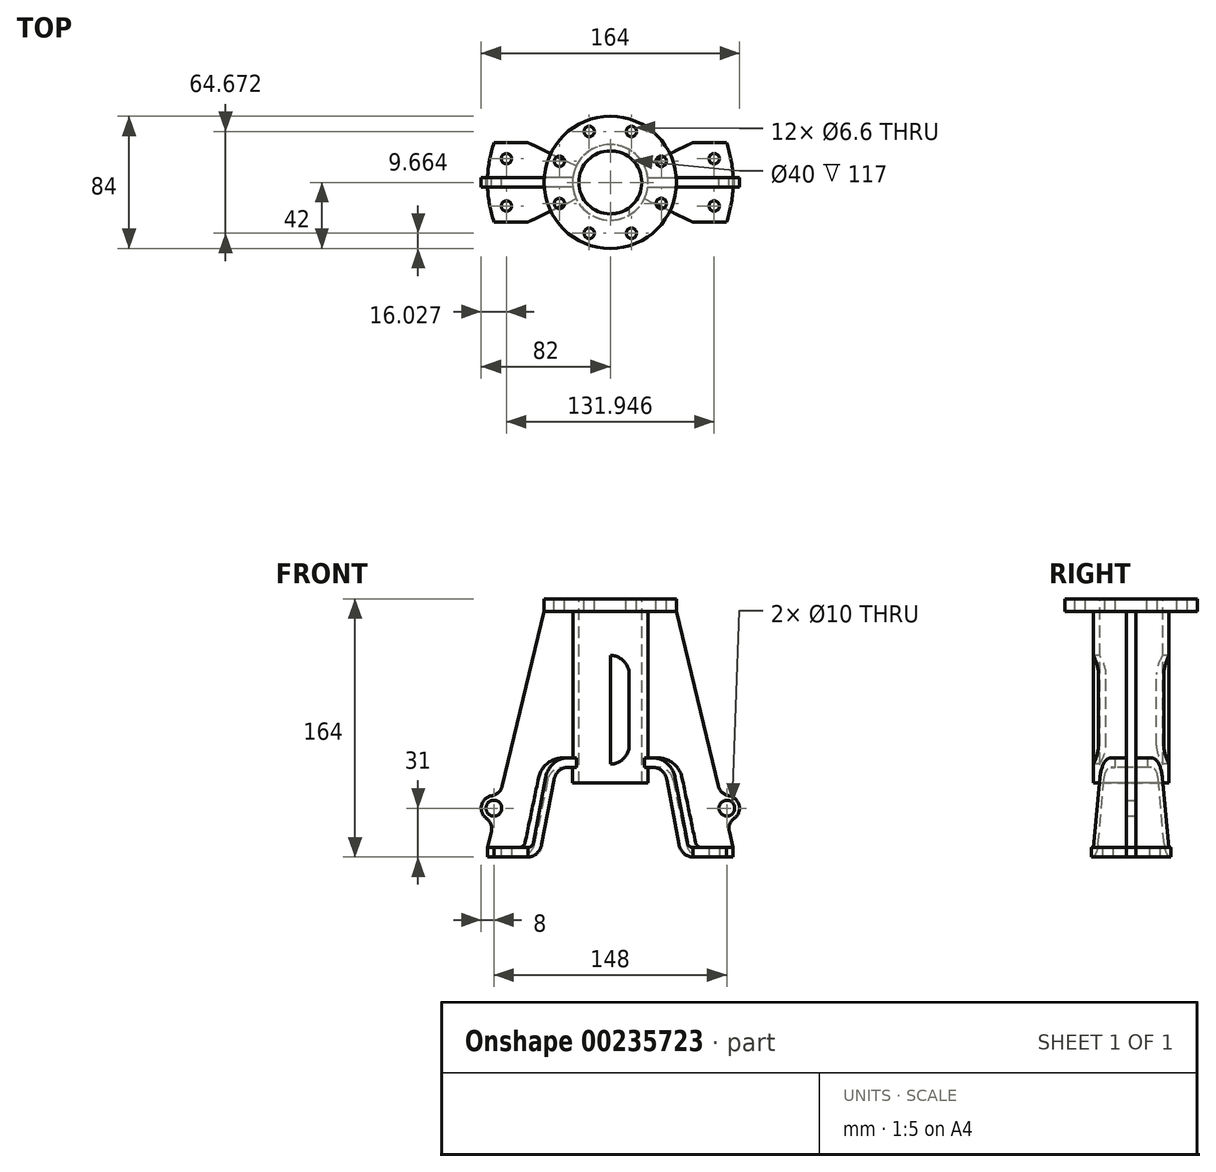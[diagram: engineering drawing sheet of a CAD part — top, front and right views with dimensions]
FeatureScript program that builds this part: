
annotation { "Feature Type Name" : "Feature", "Feature Type Description" : "" }
export const myFeature = defineFeature(function(context is Context, id is Id, definition is map)
    precondition{}
    {
        {
            var Q0;
            Q0=qCreatedBy(makeId("Front.planeOp"),FACE);
            var sketch = newSketch(context, id + "F0", { "sketchPlane" : qUnion([Q0])});
            skLineSegment(sketch, "E0.bottom", {"start": v(12, 22.5) * mm, "end": v(0, 22.5) * mm, "construction": true});
            skLineSegment(sketch, "E0.top", {"start": v(12, -22.5) * mm, "end": v(0, -22.5) * mm, "construction": true});
            skLineSegment(sketch, "E0.left", {"start": v(12, 22.5) * mm, "end": v(12, -22.5) * mm});
            skPoint(sketch, "E0.middle", {"position": v(0, 0) * mm});
            skArc(sketch, "E1", {"start": v(12, 22.5) * mm, "mid": v(8.49, 30.99) * mm, "end": v(0, 34.5) * mm});
            skArc(sketch, "E2", {"start": v(0, -34.5) * mm, "mid": v(8.49, -30.99) * mm, "end": v(12, -22.5) * mm});
            skLineSegment(sketch, "E3", {"start": v(0, 0) * mm, "end": v(0, -93.5) * mm, "construction": true});
            skPoint(sketch, "E3.endSnap0", {"position": v(0, -34.5) * mm});
            skPoint(sketch, "E4.endSnap0", {"position": v(0, 34.5) * mm});
            skLineSegment(sketch, "E5.trimOffspring", {"start": v(0, 0) * mm, "end": v(0, 70.5) * mm, "construction": true});
            skLineSegment(sketch, "E6", {"start": v(0, -93.5) * mm, "end": v(0, -36.5) * mm, "construction": true});
            skLineSegment(sketch, "E7", {"start": v(0, -93.5) * mm, "end": v(50, -93.5) * mm, "construction": true});
            skLineSegment(sketch, "E8", {"start": v(58.13, -93.5) * mm, "end": v(78, -93.5) * mm});
            skLineSegment(sketch, "E9", {"start": v(0, -36.5) * mm, "end": v(30, -36.5) * mm, "construction": true});
            skLineSegment(sketch, "E10.bottom", {"start": v(20, 70.5) * mm, "end": v(24, 70.5) * mm});
            skLineSegment(sketch, "E10.top", {"start": v(20, -46.5) * mm, "end": v(24, -46.5) * mm});
            skLineSegment(sketch, "E10.left", {"start": v(0, 70.5) * mm, "end": v(0, -46.5) * mm});
            skLineSegment(sketch, "E10.right", {"start": v(24, 70.5) * mm, "end": v(24, -46.5) * mm});
            skLineSegment(sketch, "E11.0", {"start": v(20, 70.5) * mm, "end": v(20, -46.5) * mm});
            skLineSegment(sketch, "E12", {"start": v(0, 70.5) * mm, "end": v(20, 70.5) * mm, "construction": true});
            skLineSegment(sketch, "E13", {"start": v(0, -46.5) * mm, "end": v(20, -46.5) * mm, "construction": true});
            skLineSegment(sketch, "E14.bottom", {"start": v(24, 70.5) * mm, "end": v(42, 70.5) * mm});
            skLineSegment(sketch, "E14.top", {"start": v(24, 62.5) * mm, "end": v(42, 62.5) * mm});
            skLineSegment(sketch, "E14.left", {"start": v(24, 70.5) * mm, "end": v(24, 62.5) * mm});
            skLineSegment(sketch, "E14.right", {"start": v(42, 70.5) * mm, "end": v(42, 62.5) * mm});
            skLineSegment(sketch, "E15", {"start": v(20, -46.5) * mm, "end": v(20, -46.5) * mm});
            skLineSegment(sketch, "E16", {"start": v(48.34, -85.54) * mm, "end": v(39.8, -44.46) * mm});
            skArc(sketch, "E17.trimOffspring", {"start": v(39.8, -44.46) * mm, "mid": v(36.3, -38.74) * mm, "end": v(30, -36.5) * mm});
            skPoint(sketch, "E18.visualSharp", {"position": v(50, -93.5) * mm});
            skArc(sketch, "E18.filletArc", {"start": v(48.34, -85.54) * mm, "mid": v(51.82, -91.26) * mm, "end": v(58.13, -93.5) * mm});
            skLineSegment(sketch, "E19", {"start": v(30, -36.5) * mm, "end": v(20, -36.5) * mm});
            skLineSegment(sketch, "E20.0", {"start": v(58.13, -87.5) * mm, "end": v(78, -87.5) * mm});
            skLineSegment(sketch, "E20.1", {"start": v(20, -30.5) * mm, "end": v(30, -30.5) * mm});
            skArc(sketch, "E20.2", {"start": v(45.66, -43.24) * mm, "mid": v(40.1, -34.09) * mm, "end": v(30, -30.5) * mm});
            skLineSegment(sketch, "E20.3", {"start": v(54.22, -84.32) * mm, "end": v(45.66, -43.24) * mm});
            skArc(sketch, "E20.4", {"start": v(54.22, -84.32) * mm, "mid": v(55.6, -86.6) * mm, "end": v(58.13, -87.5) * mm});
            skLineSegment(sketch, "E21", {"start": v(78, -87.5) * mm, "end": v(78, -93.5) * mm});
            skLineSegment(sketch, "E22", {"start": v(0, -93.5) * mm, "end": v(74, -93.5) * mm, "construction": true});
            skLineSegment(sketch, "E23", {"start": v(74, -93.5) * mm, "end": v(74, -62.5) * mm, "construction": true});
            skCircle(sketch, "E24", {"center": v(74, -62.5) * mm, "radius": 5 * mm});
            skLineSegment(sketch, "E25", {"start": v(42, 62.5) * mm, "end": v(68.65, -48.55) * mm});
            skLineSegment(sketch, "E26.trimOffspring", {"start": v(75.57, -77.35) * mm, "end": v(78, -87.5) * mm});
            skArc(sketch, "E27.0", {"start": v(78.67, -69) * mm, "mid": v(81.78, -60.63) * mm, "end": v(75.22, -54.6) * mm});
            skPoint(sketch, "E28.visualSharp", {"position": v(70.3, -55.4) * mm});
            skArc(sketch, "E28.filletArc", {"start": v(68.65, -48.55) * mm, "mid": v(71.01, -52.57) * mm, "end": v(75.22, -54.6) * mm});
            skPoint(sketch, "E29.visualSharp", {"position": v(73.92, -70.5) * mm});
            skArc(sketch, "E29.filletArc", {"start": v(78.67, -69) * mm, "mid": v(75.85, -72.7) * mm, "end": v(75.57, -77.35) * mm});
            skLineSegment(sketch, "E30", {"start": v(58.13, -87.5) * mm, "end": v(58.13, -93.5) * mm});
            skArc(sketch, "E31.MirrorCS", {"start": v(-12, 22.5) * mm, "mid": v(-8.49, 30.99) * mm, "end": v(0, 34.5) * mm});
            skLineSegment(sketch, "E32.MirrorCS", {"start": v(-12, 22.5) * mm, "end": v(-12, -22.5) * mm});
            skArc(sketch, "E33.MirrorCS", {"start": v(0, -34.5) * mm, "mid": v(-8.49, -30.99) * mm, "end": v(-12, -22.5) * mm});
            skSolve(sketch);
        }
        {
            var Q0;
            {var subQ1=sQuery(id+"F0.wireOp",EDGE,"E10.bottom");Q0=makeQuery(id+"F0.imprint","IMPRINT",FACE,{"disambiguationData":[TD([[makeQuery(id+"F0.imprint","IMPRINT",EDGE,{"derivedFrom":subQ1}),-1.0]])]});}
            var Q1;
            {var subQ0=sQuery(id+"F0.wireOp",EDGE,"E19");var subQ1=sQuery(id+"F0.wireOp",EDGE,"E10.right");var subQ2=makeQuery(id+"F0.imprint","INTERSECT",VERTEX,{"derivedFrom":[subQ1,subQ0]});Q1=makeQuery(id+"F0.imprint","IMPRINT",FACE,{"disambiguationData":[TD([[makeQuery(id+"F0.imprint","IMPRINT",EDGE,{"disambiguationData":[TD([[subQ2,1.0]])],"derivedFrom":subQ1}),-1.0]])]});}
            var Q2;
            {var subQ0=sQuery(id+"F0.wireOp",EDGE,"E10.top");Q2=makeQuery(id+"F0.imprint","IMPRINT",FACE,{"disambiguationData":[TD([[makeQuery(id+"F0.imprint","IMPRINT",EDGE,{"derivedFrom":subQ0}),1.0]])]});}
            var Q3;
            Q3=makeQuery(id+"F0.imprint","IMPRINT",FACE,{"disambiguationData":[TD([[makeQuery(id+"F0.imprint","IMPRINT",EDGE,{"derivedFrom":sQuery(id+"F0.wireOp",EDGE,"E14.bottom")}),-1.0]])]});
            var Q4;
            Q4=sQuery(id+"F0.wireOp",EDGE,"E10.left");
            revolve(context, id + "F1", {"entities" : qUnion([Q0, Q1, Q2, Q3]), "axis" : qUnion([Q4]), "revolveType" : RevolveType.FULL});
        }
        {
            var Q0;
            Q0=makeQuery(id+"F0.imprint","IMPRINT",FACE,{"disambiguationData":[TD([[makeQuery(id+"F0.imprint","IMPRINT",EDGE,{"derivedFrom":sQuery(id+"F0.wireOp",EDGE,"E16")}),-1.0]])]});
            var Q1;
            Q1=makeQuery(id+"F0.imprint","IMPRINT",FACE,{"disambiguationData":[TD([[makeQuery(id+"F0.imprint","IMPRINT",EDGE,{"derivedFrom":sQuery(id+"F0.wireOp",EDGE,"E8")}),1.0]])]});
            var Q2;
            Q2=sQuery(id+"F0.wireOp",EDGE,"E6");
            revolve(context, id + "F2", {"operationType" : NewBodyOperationType.ADD, "entities" : qUnion([Q0, Q1]), "axis" : qUnion([Q2]), "revolveType" : RevolveType.SYMMETRIC, "angle" : 51.4 * degree});
        }
        {
            var Q0;
            Q0=makeQuery(id+"F2.opRevolve","SWEPT_FACE",FACE,{"disambiguationData":[OSD([sQuery(id+"F0.wireOp",EDGE,"E8")])]});
            var sketch = newSketch(context, id + "F3", { "sketchPlane" : qUnion([Q0])});
            skLineSegment(sketch, "E34", {"start": v(52.38, 25.2) * mm, "end": v(73.81, 25.2) * mm});
            skLineSegment(sketch, "E35", {"start": v(73.81, 25.2) * mm, "end": v(73.81, -25.2) * mm});
            skLineSegment(sketch, "E36", {"start": v(73.81, -25.2) * mm, "end": v(52.38, -25.2) * mm});
            skLineSegment(sketch, "E37", {"start": v(58.13, 0) * mm, "end": v(73.81, 0) * mm});
            skLineSegment(sketch, "E38", {"start": v(0, 0) * mm, "end": v(65.97, 0) * mm, "construction": true});
            skLineSegment(sketch, "E39", {"start": v(65.97, 0) * mm, "end": v(65.97, 15) * mm, "construction": true});
            skLineSegment(sketch, "E40", {"start": v(65.97, 15) * mm, "end": v(65.97, -15) * mm, "construction": true});
            skSolve(sketch);
        }
        {
            var Q0;
            {var subQ0=sQuery(id+"F0.wireOp",EDGE,"E14.top");Q0=makeQuery(id+"F0.imprint","IMPRINT",FACE,{"disambiguationData":[TD([[makeQuery(id+"F0.imprint","IMPRINT",EDGE,{"derivedFrom":subQ0}),-1.0]])]});}
            var Q1;
            Q1=makeQuery(id+"F0.imprint","IMPRINT",FACE,{"disambiguationData":[TD([[makeQuery(id+"F0.imprint","IMPRINT",EDGE,{"derivedFrom":sQuery(id+"F0.wireOp",EDGE,"E16")}),-1.0]])]});
            var Q2;
            Q2=makeQuery(id+"F0.imprint","IMPRINT",FACE,{"disambiguationData":[TD([[makeQuery(id+"F0.imprint","IMPRINT",EDGE,{"derivedFrom":sQuery(id+"F0.wireOp",EDGE,"E8")}),1.0]])]});
            var Q3;
            {var subQ1=sQuery(id+"F0.wireOp",EDGE,"E10.bottom");Q3=makeQuery(id+"F0.imprint","IMPRINT",FACE,{"disambiguationData":[TD([[makeQuery(id+"F0.imprint","IMPRINT",EDGE,{"derivedFrom":subQ1}),-1.0]])]});}
            extrude(context, id + "F4", {"entities" : qUnion([Q0, Q1, Q2, Q3]), "operationType" : NewBodyOperationType.ADD, "endBound" : BoundingType.SYMMETRIC, "depth" : 6 * mm});
        }
        {
            var Q0;
            {var subQ0=sQuery(id+"F3.wireOp",EDGE,"E34");Q0=makeQuery(id+"F3.imprint","IMPRINT",FACE,{"disambiguationData":[TD([[makeQuery(id+"F3.imprint","IMPRINT",EDGE,{"derivedFrom":subQ0}),1.0]])]});}
            var Q1;
            {var subQ0=sQuery(id+"F3.wireOp",EDGE,"E36");Q1=makeQuery(id+"F3.imprint","IMPRINT",FACE,{"disambiguationData":[TD([[makeQuery(id+"F3.imprint","IMPRINT",EDGE,{"derivedFrom":subQ0}),1.0]])]});}
            extrude(context, id + "F5", {"entities" : qUnion([Q0, Q1]), "operationType" : NewBodyOperationType.REMOVE, "oppositeDirection" : true, "depth" : 25 * mm});
        }
        {
            var Q0;
            Q0=sQuery(id+"F3.wireOp",VERTEX,"E40.start");
            var Q1;
            Q1=sQuery(id+"F3.wireOp",VERTEX,"E40.end");
            var Q2;
            Q2=makeQuery(id+"F1.opRevolve","SWEPT_BODY",BODY,{"disambiguationData":[OSD([sQuery(id+"F0.wireOp",EDGE,"E10.bottom"),sQuery(id+"F0.wireOp",EDGE,"E10.top"),sQuery(id+"F0.wireOp",EDGE,"E10.right"),sQuery(id+"F0.wireOp",EDGE,"E11.0"),sQuery(id+"F0.wireOp",EDGE,"E14.bottom"),sQuery(id+"F0.wireOp",EDGE,"E14.top"),sQuery(id+"F0.wireOp",EDGE,"E14.right")])]});
            hole(context, id + "F6", {"style" : HoleStyle.SIMPLE, "endStyle" : HoleEndStyle.THROUGH, "standardTappedOrClearance" : lookupTablePath({ "standard" : "ISO", "fit" : "Normal", "size" : "M6", "type" : "Clearance" }), "standardBlindInLast" : lookupTablePath({ "fit" : "Standard", "standard" : "ISO", "size" : "M6", "type" : "Clearance" }), "holeDiameter" : 6.6 * mm, "isTappedThrough" : true, "tappedDepth" : 9 * mm, "tapClearance" : 3, "startFromSketch" : true, "locations" : qUnion([Q0, Q1]), "scope" : qUnion([Q2])});
        }
        {
            var Q0;
            Q0=makeQuery(id+"F1.opRevolve","SWEPT_BODY",BODY,{"disambiguationData":[OSD([sQuery(id+"F0.wireOp",EDGE,"E10.bottom"),sQuery(id+"F0.wireOp",EDGE,"E10.top"),sQuery(id+"F0.wireOp",EDGE,"E10.right"),sQuery(id+"F0.wireOp",EDGE,"E11.0"),sQuery(id+"F0.wireOp",EDGE,"E14.bottom"),sQuery(id+"F0.wireOp",EDGE,"E14.top"),sQuery(id+"F0.wireOp",EDGE,"E14.right")])]});
            var Q1;
            Q1=qCreatedBy(makeId("Right.planeOp"),FACE);
            mirror(context, id + "F7", {"operationType" : NewBodyOperationType.ADD, "entities" : qUnion([Q0]), "mirrorPlane" : qUnion([Q1])});
        }
        {
            var Q0;
            {var subQ0=sQuery(id+"F0.wireOp",EDGE,"E31.MirrorCS");Q0=makeQuery(id+"F0.imprint","IMPRINT",FACE,{"disambiguationData":[TD([[makeQuery(id+"F0.imprint","IMPRINT",EDGE,{"derivedFrom":subQ0}),-1.0]])]});}
            var Q1;
            Q1=makeQuery(id+"F0.imprint","IMPRINT",FACE,{"disambiguationData":[TD([[makeQuery(id+"F0.imprint","IMPRINT",EDGE,{"derivedFrom":sQuery(id+"F0.wireOp",EDGE,"E0.left")}),-1.0]])]});
            extrude(context, id + "F8", {"entities" : qUnion([Q0, Q1]), "operationType" : NewBodyOperationType.REMOVE, "endBound" : BoundingType.SYMMETRIC, "oppositeDirection" : true, "depth" : 48 * mm});
        }
        {
            var Q0;
            Q0=makeQuery(id+"F1.opRevolve","SWEPT_FACE",FACE,{"disambiguationData":[OSD([sQuery(id+"F0.wireOp",EDGE,"E10.bottom"),sQuery(id+"F0.wireOp",EDGE,"E14.bottom")])]});
            var sketch = newSketch(context, id + "F9", { "sketchPlane" : qUnion([Q0])});
            skLineSegment(sketch, "E41", {"start": v(0, 0) * mm, "end": v(0, 42) * mm, "construction": true});
            skLineSegment(sketch, "E42", {"start": v(0, 0) * mm, "end": v(16.07, 38.8) * mm, "construction": true});
            skCircle(sketch, "E43", {"center": v(0, 0) * mm, "radius": 35 * mm, "construction": true});
            skLineSegment(sketch, "E44.1.0", {"start": v(0, 0) * mm, "end": v(-16.07, 38.8) * mm, "construction": true});
            skLineSegment(sketch, "E44.2.0", {"start": v(0, 0) * mm, "end": v(-38.8, 16.07) * mm, "construction": true});
            skLineSegment(sketch, "E44.3.0", {"start": v(0, 0) * mm, "end": v(-38.8, -16.07) * mm, "construction": true});
            skLineSegment(sketch, "E44.4.0", {"start": v(0, 0) * mm, "end": v(-16.07, -38.8) * mm, "construction": true});
            skLineSegment(sketch, "E44.5.0", {"start": v(0, 0) * mm, "end": v(16.07, -38.8) * mm, "construction": true});
            skLineSegment(sketch, "E44.6.0", {"start": v(0, 0) * mm, "end": v(38.8, -16.07) * mm, "construction": true});
            skLineSegment(sketch, "E44.7.0", {"start": v(0, 0) * mm, "end": v(38.8, 16.07) * mm, "construction": true});
            skCircle(sketch, "E45", {"center": v(-13.4, 32.34) * mm, "radius": 2.32 * mm});
            skCircle(sketch, "E46", {"center": v(13.4, 32.34) * mm, "radius": 3.04 * mm});
            skCircle(sketch, "E47", {"center": v(-32.34, 13.4) * mm, "radius": 2.69 * mm});
            skCircle(sketch, "E48", {"center": v(-32.34, -13.4) * mm, "radius": 2.5 * mm});
            skCircle(sketch, "E49", {"center": v(-13.4, -32.34) * mm, "radius": 2.26 * mm});
            skCircle(sketch, "E50", {"center": v(13.4, -32.34) * mm, "radius": 2.36 * mm});
            skCircle(sketch, "E51", {"center": v(32.34, -13.4) * mm, "radius": 2.72 * mm});
            skCircle(sketch, "E52", {"center": v(32.34, 13.4) * mm, "radius": 3.38 * mm});
            skSolve(sketch);
        }
        {
            var Q0;
            Q0=sQuery(id+"F9.wireOp",VERTEX,"E45.center");
            var Q1;
            Q1=sQuery(id+"F9.wireOp",VERTEX,"E46.center");
            var Q2;
            Q2=sQuery(id+"F9.wireOp",VERTEX,"E52.center");
            var Q3;
            Q3=sQuery(id+"F9.wireOp",VERTEX,"E51.center");
            var Q4;
            Q4=sQuery(id+"F9.wireOp",VERTEX,"E50.center");
            var Q5;
            Q5=sQuery(id+"F9.wireOp",VERTEX,"E49.center");
            var Q6;
            Q6=sQuery(id+"F9.wireOp",VERTEX,"E48.center");
            var Q7;
            Q7=sQuery(id+"F9.wireOp",VERTEX,"E47.center");
            var Q8;
            Q8=makeQuery(id+"F1.opRevolve","SWEPT_BODY",BODY,{"disambiguationData":[OSD([sQuery(id+"F0.wireOp",EDGE,"E10.bottom"),sQuery(id+"F0.wireOp",EDGE,"E10.top"),sQuery(id+"F0.wireOp",EDGE,"E10.right"),sQuery(id+"F0.wireOp",EDGE,"E11.0"),sQuery(id+"F0.wireOp",EDGE,"E14.bottom"),sQuery(id+"F0.wireOp",EDGE,"E14.top"),sQuery(id+"F0.wireOp",EDGE,"E14.right")])]});
            hole(context, id + "F10", {"style" : HoleStyle.SIMPLE, "endStyle" : HoleEndStyle.BLIND, "standardTappedOrClearance" : lookupTablePath({ "standard" : "ISO", "fit" : "Normal", "size" : "M6", "type" : "Clearance" }), "standardBlindInLast" : lookupTablePath({ "fit" : "Standard", "standard" : "ISO", "size" : "M6", "type" : "Clearance" }), "holeDiameter" : 6.6 * mm, "holeDepth" : 11.25 * mm, "isTappedThrough" : true, "tappedDepth" : 9 * mm, "tapClearance" : 3, "startFromSketch" : true, "locations" : qUnion([Q0, Q1, Q2, Q3, Q4, Q5, Q6, Q7]), "scope" : qUnion([Q8])});
        }
    });
